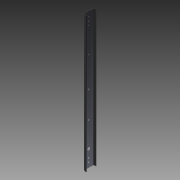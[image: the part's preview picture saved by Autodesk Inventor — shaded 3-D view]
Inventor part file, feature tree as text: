
AUTODESK INVENTOR PART (.ipt)
format: ipt  version: 2011 SP1 (Build 150282100, 282)  size: 154,112 bytes
history: native  units: mm
features: sketch x10, extrude x9, other x7, hole x1
ambient origin geometry x8: Origin, YZ Plane, XZ Plane, XY Plane, X Axis, Y Axis, Z Axis, Center Point
bodies: Solid1 (feature_tree)
feature tree (27):
  extrude  "Extrusion1"  Depth=0.5mm TaperAngle=0.0deg
  extrude  "Extrusion2"  Depth=0.5mm TaperAngle=0.0deg
  extrude  "Extrusion3"  Depth=0.5mm TaperAngle=0.0deg
  extrude  "Extrusion4"  Depth=0.5mm TaperAngle=0.0deg
  extrude  "Extrusion5"  [1 undecoded]
  extrude  "Extrusion6"  [1 undecoded]
  extrude  "Extrusion7"  [1 undecoded]
  extrude  "Extrusion8"  [1 undecoded]
  extrude  "Extrusion9"  [1 undecoded]
  hole  "Hole1"  [1 undecoded]
  other  "to_rail_XY"
  other  "to_rail_YZ"
  other  "to_rail_ZX"
  other  "to_rail_X"
  other  "to_rail_Y"
  other  "to_rail_Z"
  other  "to_rail_Center"
  sketch  "Sketch_1"  dims[d0=457.2mm d1=0.0mm d2=0.5mm d3=0.0mm]
  sketch  "Sketch_4"  dims[d8=0.5mm d9=0.0mm d10=0.5mm d11=0.0mm]
  sketch  "Sketch_5"  dims[d12=0.5mm d13=0.0mm d14=0.5mm d15=0.0mm]
  sketch  "Sketch_6"  dims[d16=0.5mm d17=0.0mm]
  sketch  "Sketch_7"  dims[d18=9.5mm d19=6.0mm d20=4.0mm d21=2.0mm d22=90.0deg d23=0.5mm d24=0.0mm]
  sketch  "Sketch_3"  dims[d4=0.5mm d5=0.0mm d6=0.5mm d7=0.0mm]
  sketch  "Sketch_8"
  sketch  "Sketch_9"
  sketch  "Sketch_10"
  sketch  "Sketch10"
note: 6 required parameter values undecoded (feature->parameter linkage not recoverable at this tier; creation-order binding heuristic only, values carry confidence <= 0.55)
